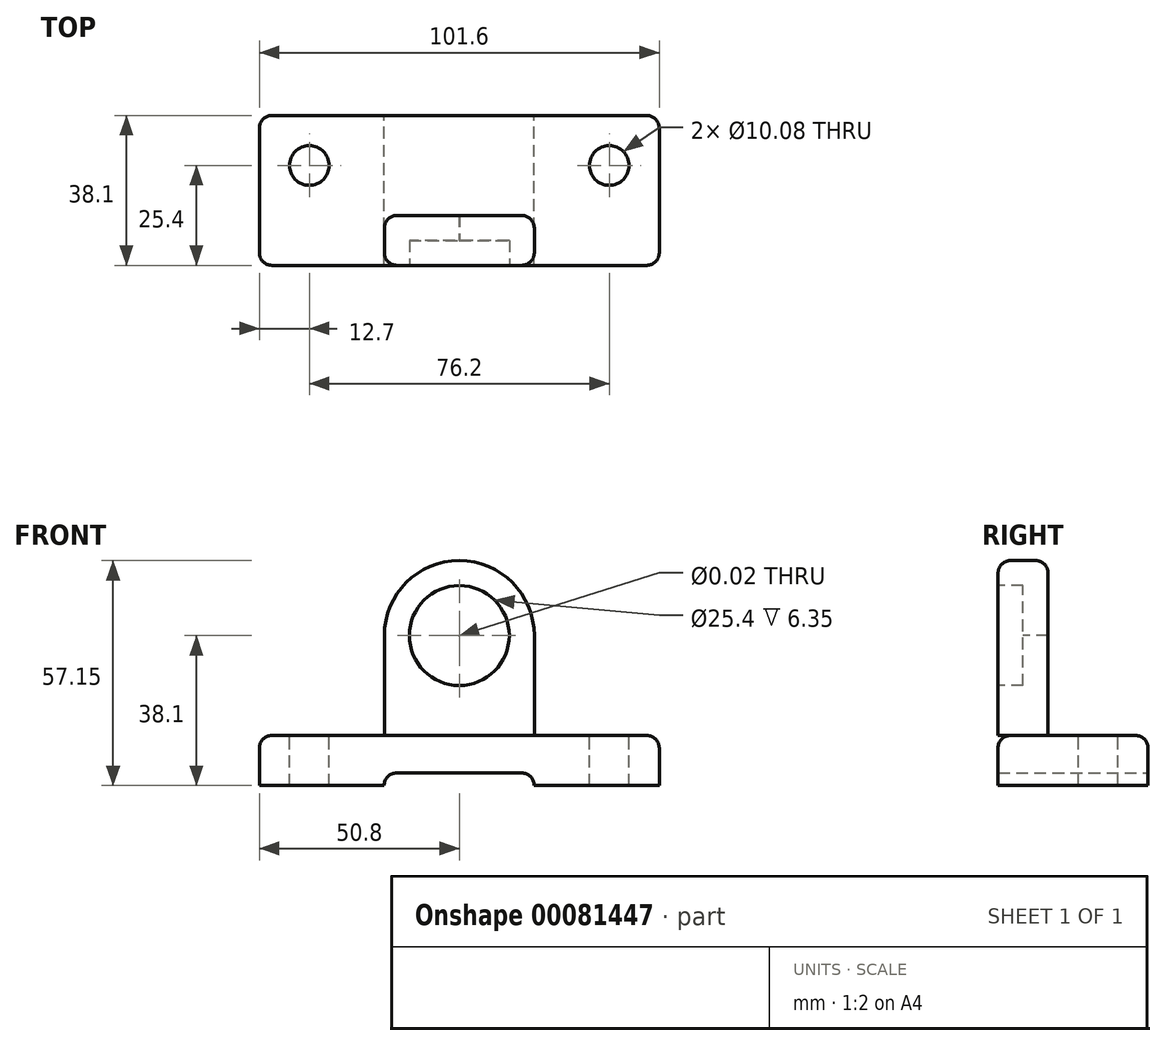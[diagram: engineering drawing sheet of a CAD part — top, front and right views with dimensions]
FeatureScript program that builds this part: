
annotation { "Feature Type Name" : "Feature", "Feature Type Description" : "" }
export const myFeature = defineFeature(function(context is Context, id is Id, definition is map)
    precondition{}
    {
        {
            var Q0;
            Q0=qCreatedBy(makeId("Top.planeOp"),FACE);
            var sketch = newSketch(context, id + "F0", { "sketchPlane" : qUnion([Q0])});
            skLineSegment(sketch, "E0.bottom", {"start": v(-50.8, 19.05) * mm, "end": v(50.8, 19.05) * mm});
            skLineSegment(sketch, "E0.top", {"start": v(-50.8, -19.05) * mm, "end": v(50.8, -19.05) * mm});
            skLineSegment(sketch, "E0.left", {"start": v(-50.8, 19.05) * mm, "end": v(-50.8, -19.05) * mm});
            skLineSegment(sketch, "E0.right", {"start": v(50.8, 19.05) * mm, "end": v(50.8, -19.05) * mm});
            skPoint(sketch, "E0.middle", {"position": v(0, 0) * mm});
            skSolve(sketch);
        }
        {
            var Q0;
            Q0=makeQuery(id+"F0.imprint","IMPRINT",FACE,{"disambiguationData":[TD([[makeQuery(id+"F0.imprint","IMPRINT",EDGE,{"derivedFrom":sQuery(id+"F0.wireOp",EDGE,"E0.bottom")}),-1.0]])]});
            extrude(context, id + "F1", {"entities" : qUnion([Q0]), "depth" : 12.7 * mm});
        }
        {
            var Q0;
            Q0=makeQuery(id+"F1.opExtrude","SWEPT_FACE",FACE,{"disambiguationData":[OSD([sQuery(id+"F0.wireOp",EDGE,"E0.top")])]});
            var sketch = newSketch(context, id + "F2", { "sketchPlane" : qUnion([Q0])});
            skLineSegment(sketch, "E1", {"start": v(-19.05, 0) * mm, "end": v(-19.05, 38.1) * mm});
            skArc(sketch, "E2", {"start": v(19.05, 38.1) * mm, "mid": v(0, 57.15) * mm, "end": v(-19.05, 38.1) * mm});
            skLineSegment(sketch, "E3", {"start": v(19.05, 38.1) * mm, "end": v(19.05, 0) * mm});
            skSolve(sketch);
        }
        {
            var Q0;
            {var subQ0=sQuery(id+"F2.wireOp",EDGE,"E2");Q0=makeQuery(id+"F2.imprint","IMPRINT",FACE,{"disambiguationData":[TD([[makeQuery(id+"F2.imprint","IMPRINT",EDGE,{"derivedFrom":subQ0}),1.0]])]});}
            extrude(context, id + "F3", {"entities" : qUnion([Q0]), "oppositeDirection" : true, "depth" : 12.7 * mm});
        }
        {
            var Q0;
            Q0=makeQuery(id+"F3.opExtrude","CAP_FACE",FACE,{"disambiguationData":[OSD([sQuery(id+"F0.wireOp",EDGE,"E0.top"),sQuery(id+"F2.wireOp",EDGE,"E1"),sQuery(id+"F2.wireOp",EDGE,"E2"),sQuery(id+"F2.wireOp",EDGE,"E3")])],"isStart":true});
            var sketch = newSketch(context, id + "F4", { "sketchPlane" : qUnion([Q0])});
            skCircle(sketch, "E4", {"center": v(0, 38.1) * mm, "radius": 7.24 * mm});
            skSolve(sketch);
        }
        {
            var Q0;
            Q0=sQuery(id+"F4.wireOp",VERTEX,"E4.center");
            var Q1;
            Q1=makeQuery(id+"F3.opExtrude","SWEPT_BODY",BODY,{"disambiguationData":[OSD([sQuery(id+"F0.wireOp",EDGE,"E0.top"),sQuery(id+"F2.wireOp",EDGE,"E1"),sQuery(id+"F2.wireOp",EDGE,"E2"),sQuery(id+"F2.wireOp",EDGE,"E3")])]});
            hole(context, id + "F5", {"style" : HoleStyle.C_BORE, "endStyle" : HoleEndStyle.THROUGH, "standardTappedOrClearance" : lookupTablePath({ "standard" : "ANSI", "size" : "15/32 (0.47)", "type" : "Drilled" }), "standardBlindInLast" : lookupTablePath({ "standard" : "ANSI", "size" : "15/32", "type" : "Drilled" }), "holeDiameter" : 15 / 812.8 * mm, "cBoreDiameter" : 25.4 * mm, "cBoreDepth" : 6.35 * mm, "locations" : qUnion([Q0]), "scope" : qUnion([Q1]), "isTappedThrough" : true});
        }
        {
            var Q0;
            Q0=makeQuery(id+"F1.opExtrude","SWEPT_FACE",FACE,{"disambiguationData":[OSD([sQuery(id+"F0.wireOp",EDGE,"E0.bottom")])]});
            var sketch = newSketch(context, id + "F6", { "sketchPlane" : qUnion([Q0])});
            skLineSegment(sketch, "E5", {"start": v(-19.02, 3.17) * mm, "end": v(19.08, 3.18) * mm});
            skLineSegment(sketch, "E6", {"start": v(-19.02, 3.17) * mm, "end": v(-19.02, 0) * mm});
            skLineSegment(sketch, "E7", {"start": v(19.08, 3.18) * mm, "end": v(19.08, 0) * mm});
            skLineSegment(sketch, "E8", {"start": v(19.08, 0) * mm, "end": v(-19.02, 0) * mm});
            skSolve(sketch);
        }
        {
            var Q0;
            Q0=makeQuery(id+"F6.imprint","IMPRINT",FACE,{"disambiguationData":[TD([[makeQuery(id+"F6.imprint","IMPRINT",EDGE,{"derivedFrom":sQuery(id+"F6.wireOp",EDGE,"E5")}),-1.0]])]});
            extrude(context, id + "F7", {"entities" : qUnion([Q0]), "operationType" : NewBodyOperationType.REMOVE, "endBound" : BoundingType.THROUGH_ALL, "oppositeDirection" : true, "depth" : 25.4 * mm});
        }
        {
            var Q0;
            Q0=makeQuery(id+"F1.opExtrude","CAP_FACE",FACE,{"disambiguationData":[OSD([sQuery(id+"F0.wireOp",EDGE,"E0.bottom"),sQuery(id+"F0.wireOp",EDGE,"E0.top"),sQuery(id+"F0.wireOp",EDGE,"E0.left"),sQuery(id+"F0.wireOp",EDGE,"E0.right")])],"isStart":false});
            var sketch = newSketch(context, id + "F8", { "sketchPlane" : qUnion([Q0])});
            skCircle(sketch, "E9", {"center": v(-38.1, 6.35) * mm, "radius": 3.96 * mm});
            skCircle(sketch, "E10", {"center": v(38.1, 6.35) * mm, "radius": 4.04 * mm});
            skSolve(sketch);
        }
        {
            var Q0;
            Q0=sQuery(id+"F8.wireOp",VERTEX,"E9.center");
            var Q1;
            Q1=makeQuery(id+"F1.opExtrude","SWEPT_BODY",BODY,{"disambiguationData":[OSD([sQuery(id+"F0.wireOp",EDGE,"E0.bottom"),sQuery(id+"F0.wireOp",EDGE,"E0.top"),sQuery(id+"F0.wireOp",EDGE,"E0.left"),sQuery(id+"F0.wireOp",EDGE,"E0.right")])]});
            hole(context, id + "F9", {"style" : HoleStyle.SIMPLE, "endStyle" : HoleEndStyle.THROUGH, "standardTappedOrClearance" : lookupTablePath({ "standard" : "ANSI", "fit" : "Normal (ASME)", "size" : "3/8", "type" : "Clearance" }), "standardBlindInLast" : lookupTablePath({ "fit" : "Free", "standard" : "ANSI", "size" : "3/8", "type" : "Clearance" }), "holeDiameter" : 10.08 * mm, "locations" : qUnion([Q0]), "scope" : qUnion([Q1]), "isTappedThrough" : true});
        }
        {
            var Q0;
            Q0=sQuery(id+"F8.wireOp",VERTEX,"E10.center");
            var Q1;
            Q1=makeQuery(id+"F1.opExtrude","SWEPT_BODY",BODY,{"disambiguationData":[OSD([sQuery(id+"F0.wireOp",EDGE,"E0.bottom"),sQuery(id+"F0.wireOp",EDGE,"E0.top"),sQuery(id+"F0.wireOp",EDGE,"E0.left"),sQuery(id+"F0.wireOp",EDGE,"E0.right")])]});
            hole(context, id + "F10", {"style" : HoleStyle.SIMPLE, "endStyle" : HoleEndStyle.THROUGH, "standardTappedOrClearance" : lookupTablePath({ "standard" : "ANSI", "fit" : "Normal (ASME)", "size" : "3/8", "type" : "Clearance" }), "standardBlindInLast" : lookupTablePath({ "fit" : "Free", "standard" : "ANSI", "size" : "3/8", "type" : "Clearance" }), "holeDiameter" : 10.08 * mm, "locations" : qUnion([Q0]), "scope" : qUnion([Q1]), "isTappedThrough" : true});
        }
        {
            var Q0;
            Q0=makeQuery(id+"F1.opExtrude","SWEPT_EDGE",EDGE,{"disambiguationData":[OSD([sQuery(id+"F0.wireOp",EDGE,"E0.top"),sQuery(id+"F0.wireOp",EDGE,"E0.right")])]});
            var Q1;
            Q1=makeQuery(id+"F1.opExtrude","SWEPT_EDGE",EDGE,{"disambiguationData":[OSD([sQuery(id+"F0.wireOp",EDGE,"E0.bottom"),sQuery(id+"F0.wireOp",EDGE,"E0.right")])]});
            var Q2;
            Q2=makeQuery(id+"F1.opExtrude","SWEPT_EDGE",EDGE,{"disambiguationData":[OSD([sQuery(id+"F0.wireOp",EDGE,"E0.top"),sQuery(id+"F0.wireOp",EDGE,"E0.left")])]});
            var Q3;
            Q3=makeQuery(id+"F1.opExtrude","SWEPT_EDGE",EDGE,{"disambiguationData":[OSD([sQuery(id+"F0.wireOp",EDGE,"E0.bottom"),sQuery(id+"F0.wireOp",EDGE,"E0.left")])]});
            fillet(context, id + "F11", {"entities" : qUnion([Q0, Q1, Q2, Q3]), "radius" : 3.17 * mm, "tangentPropagation" : true, "allowEdgeOverflow" : false});
        }
        {
            var Q0;
            Q0=makeQuery(id+"F7.boolean.opBoolean","COPY",EDGE,{"derivedFrom":makeQuery(id+"F7.opExtrude","SWEPT_EDGE",EDGE,{"disambiguationData":[OSD([sQuery(id+"F6.wireOp",EDGE,"E5"),sQuery(id+"F6.wireOp",EDGE,"E6")])]})});
            var Q1;
            Q1=makeQuery(id+"F7.boolean.opBoolean","COPY",EDGE,{"derivedFrom":makeQuery(id+"F7.opExtrude","SWEPT_EDGE",EDGE,{"disambiguationData":[OSD([sQuery(id+"F6.wireOp",EDGE,"E5"),sQuery(id+"F6.wireOp",EDGE,"E7")])]})});
            var Q2;
            Q2=makeQuery(id+"F1.opExtrude","CAP_EDGE",EDGE,{"disambiguationData":[OSD([sQuery(id+"F0.wireOp",EDGE,"E0.bottom")])],"isStart":false});
            var Q3;
            Q3=makeQuery(id+"F3.opExtrude","CAP_EDGE",EDGE,{"disambiguationData":[OSD([sQuery(id+"F2.wireOp",EDGE,"E2")])],"isStart":true});
            var Q4;
            Q4=makeQuery(id+"F3.opExtrude","CAP_EDGE",EDGE,{"disambiguationData":[OSD([sQuery(id+"F2.wireOp",EDGE,"E2")])],"isStart":false});
            var Q5;
            Q5=makeQuery(id+"F3.opExtrude","CAP_EDGE",EDGE,{"disambiguationData":[OSD([sQuery(id+"F2.wireOp",EDGE,"E3")])],"isStart":true});
            var Q6;
            Q6=makeQuery(id+"F3.opExtrude","CAP_EDGE",EDGE,{"disambiguationData":[OSD([sQuery(id+"F2.wireOp",EDGE,"E3")])],"isStart":false});
            var Q7;
            Q7=makeQuery(id+"F3.opExtrude","CAP_EDGE",EDGE,{"disambiguationData":[OSD([sQuery(id+"F2.wireOp",EDGE,"E1")])],"isStart":true});
            var Q8;
            Q8=makeQuery(id+"F3.opExtrude","CAP_EDGE",EDGE,{"disambiguationData":[OSD([sQuery(id+"F2.wireOp",EDGE,"E1")])],"isStart":false});
            fillet(context, id + "F12", {"entities" : qUnion([Q0, Q1, Q2, Q3, Q4, Q5, Q6, Q7, Q8]), "radius" : 3.17 * mm, "tangentPropagation" : true, "allowEdgeOverflow" : false});
        }
    });
